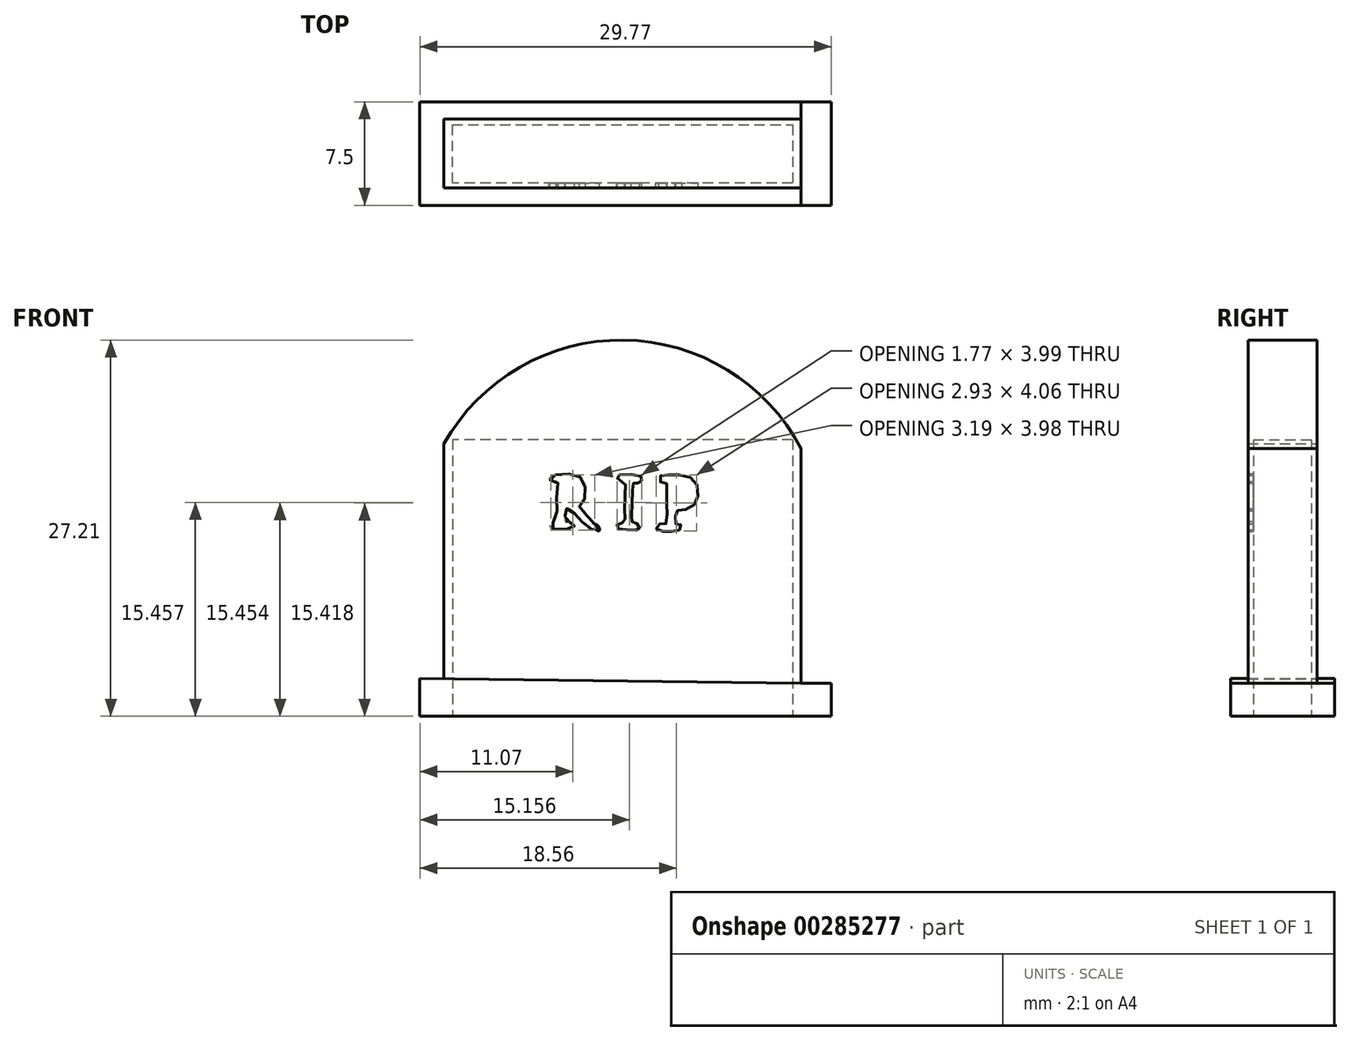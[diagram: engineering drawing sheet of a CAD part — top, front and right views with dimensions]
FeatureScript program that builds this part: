
annotation { "Feature Type Name" : "Feature", "Feature Type Description" : "" }
export const myFeature = defineFeature(function(context is Context, id is Id, definition is map)
    precondition{}
    {
        {
            var Q0;
            Q0=qCreatedBy(makeId("Front.planeOp"),FACE);
            var sketch = newSketch(context, id + "F0", { "sketchPlane" : qUnion([Q0])});
            skArc(sketch, "E0", {"start": v(30.22, 31.46) * mm, "mid": v(17.4, 39.29) * mm, "end": v(4.38, 31.78) * mm});
            skLineSegment(sketch, "E1", {"start": v(4.38, 31.78) * mm, "end": v(4.38, 14.78) * mm});
            skLineSegment(sketch, "E2", {"start": v(30.22, 31.46) * mm, "end": v(30.22, 14.46) * mm});
            skLineSegment(sketch, "E3", {"start": v(4.38, 14.78) * mm, "end": v(30.22, 14.46) * mm});
            skLineSegment(sketch, "E4", {"start": v(4.38, 14.78) * mm, "end": v(2.65, 14.8) * mm});
            skLineSegment(sketch, "E5", {"start": v(2.65, 14.8) * mm, "end": v(2.65, 12.08) * mm});
            skLineSegment(sketch, "E6", {"start": v(2.65, 12.08) * mm, "end": v(32.42, 12.08) * mm});
            skLineSegment(sketch, "E7", {"start": v(32.42, 12.08) * mm, "end": v(32.42, 14.46) * mm});
            skLineSegment(sketch, "E8", {"start": v(32.42, 14.46) * mm, "end": v(30.22, 14.46) * mm});
            skSolve(sketch);
        }
        {
            var Q0;
            Q0=makeQuery(id+"F0.imprint","IMPRINT",FACE,{"disambiguationData":[TD([[makeQuery(id+"F0.imprint","IMPRINT",EDGE,{"derivedFrom":sQuery(id+"F0.wireOp",EDGE,"E0")}),1.0]])]});
            extrude(context, id + "F1", {"entities" : qUnion([Q0]), "endBound" : BoundingType.SYMMETRIC, "depth" : 5 * mm});
        }
        {
            var Q0;
            Q0=makeQuery(id+"F0.imprint","IMPRINT",FACE,{"disambiguationData":[TD([[makeQuery(id+"F0.imprint","IMPRINT",EDGE,{"derivedFrom":sQuery(id+"F0.wireOp",EDGE,"E3")}),-1.0]])]});
            extrude(context, id + "F2", {"entities" : qUnion([Q0]), "operationType" : NewBodyOperationType.ADD, "endBound" : BoundingType.SYMMETRIC, "depth" : 7.5 * mm});
        }
        {
            var Q0;
            Q0=makeQuery(id+"F2.opExtrude","SWEPT_FACE",FACE,{"disambiguationData":[OSD([sQuery(id+"F0.wireOp",EDGE,"E6")])]});
            var sketch = newSketch(context, id + "F3", { "sketchPlane" : qUnion([Q0])});
            skLineSegment(sketch, "E9", {"start": v(5, 1.52) * mm, "end": v(5, -2.08) * mm});
            skLineSegment(sketch, "E10", {"start": v(5, -2.08) * mm, "end": v(29.62, -2.08) * mm});
            skLineSegment(sketch, "E11", {"start": v(29.62, -2.08) * mm, "end": v(29.62, 2.13) * mm});
            skLineSegment(sketch, "E12", {"start": v(29.62, 2.13) * mm, "end": v(5, 2.13) * mm});
            skLineSegment(sketch, "E13", {"start": v(5, 2.13) * mm, "end": v(5, 1.52) * mm});
            skSolve(sketch);
        }
        {
            var Q0;
            Q0 = qSketchRegion(id + "F3", true);
            extrude(context, id + "F4", {"entities" : qUnion([Q0]), "operationType" : NewBodyOperationType.REMOVE, "oppositeDirection" : true, "depth" : 20 * mm});
        }
        {
            var Q0;
            Q0=makeQuery(id+"F1.opExtrude","CAP_FACE",FACE,{"disambiguationData":[OSD([sQuery(id+"F0.wireOp",EDGE,"E0"),sQuery(id+"F0.wireOp",EDGE,"E1"),sQuery(id+"F0.wireOp",EDGE,"E2"),sQuery(id+"F0.wireOp",EDGE,"E3")])],"isStart":false});
            var sketch = newSketch(context, id + "F5", { "sketchPlane" : qUnion([Q0])});
            skFitSpline(sketch, "E14", {"points": [v(12.45, 29.53) * mm, v(13.37, 29.62) * mm, v(14.15, 29.44) * mm, v(14.52, 28.99) * mm, v(14.64, 28.26) * mm, v(14.5, 27.62) * mm, v(14.19, 27.25) * mm, v(14.18, 27.21) * mm, v(14.77, 26.53) * mm, v(15.14, 26.1) * mm, v(15.57, 25.81) * mm, v(15.63, 25.5) * mm, v(15.27, 25.56) * mm, v(14.85, 25.67) * mm, v(14.16, 26.4) * mm, v(13.82, 26.77) * mm, v(13.47, 27.08) * mm, v(13.18, 27.08) * mm, v(13.18, 27) * mm, v(13.15, 26.2) * mm, v(13.28, 26.19) * mm, v(13.7, 26.06) * mm, v(13.84, 25.84) * mm, v(13.66, 25.72) * mm, v(13.18, 25.58) * mm, v(12.24, 25.66) * mm, v(12.08, 25.92) * mm, v(12.41, 26.2) * mm, v(12.55, 27.1) * mm, v(12.54, 28.05) * mm, v(12.61, 29.02) * mm, v(12.24, 29.08) * mm, v(12.01, 29.29) * mm, v(12.45, 29.53) * mm]});
            skFitSpline(sketch, "E15", {"points": [v(17.08, 29.53) * mm, v(18.57, 29.46) * mm, v(18.68, 29.3) * mm, v(18.64, 29) * mm, v(18.28, 28.96) * mm, v(18.12, 28.97) * mm, v(18.05, 28.7) * mm, v(17.97, 26.8) * mm, v(18, 26.15) * mm, v(18.21, 26.06) * mm, v(18.53, 25.9) * mm, v(18.47, 25.55) * mm, v(18.08, 25.57) * mm, v(17.05, 25.62) * mm, v(16.9, 25.8) * mm, v(17, 26.03) * mm, v(17.43, 26.12) * mm, v(17.47, 26.47) * mm, v(17.51, 28.38) * mm, v(17.47, 28.98) * mm, v(17.12, 29.08) * mm, v(16.92, 29.37) * mm, v(17.08, 29.53) * mm]});
            skFitSpline(sketch, "E16", {"points": [v(20.59, 29.53) * mm, v(20.14, 29.53) * mm, v(19.93, 29.17) * mm, v(20.2, 28.98) * mm, v(20.48, 28.93) * mm, v(20.53, 28.25) * mm, v(20.5, 27.41) * mm, v(20.55, 26.66) * mm, v(20.45, 26) * mm, v(20.28, 26) * mm, v(19.86, 25.93) * mm, v(19.74, 25.67) * mm, v(20.06, 25.49) * mm, v(20.48, 25.44) * mm, v(21.03, 25.45) * mm, v(21.48, 25.6) * mm, v(21.6, 25.84) * mm, v(21.33, 25.98) * mm, v(21.17, 25.98) * mm, v(21.17, 26.13) * mm, v(21.13, 26.77) * mm, v(21.25, 26.95) * mm, v(21.52, 26.94) * mm, v(22.27, 27.2) * mm, v(22.67, 27.65) * mm, v(22.77, 28.54) * mm, v(22.45, 29.2) * mm, v(21.58, 29.53) * mm, v(20.59, 29.53) * mm]});
            skSolve(sketch);
        }
        {
            var Q0;
            Q0 = qSketchRegion(id + "F5", true);
            extrude(context, id + "F6", {"entities" : qUnion([Q0]), "operationType" : NewBodyOperationType.REMOVE, "oppositeDirection" : true, "depth" : 1 * mm});
        }
    });
